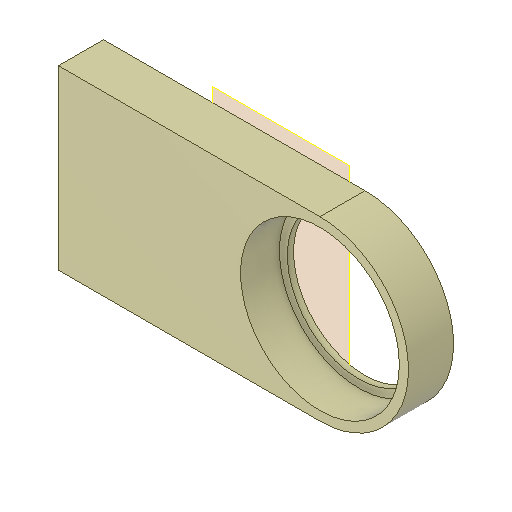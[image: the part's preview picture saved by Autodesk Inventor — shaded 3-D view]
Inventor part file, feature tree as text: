
AUTODESK INVENTOR PART (.ipt)
format: ipt  version: 2022.5 (Build 265521000, 521)  size: 133,632 bytes
history: native  units: mm
features: extrude x2, sketch x2, reference x2, other x2, plane x1, projected_geometry x1
ambient origin geometry x8: Origin, YZ Plane, XZ Plane, XY Plane, X Axis, Y Axis, Z Axis, Center Point
bodies: Solid1 (feature_tree)
feature tree (10):
  plane  "Work Plane1"
  extrude  "Extrusion1"  Depth=25.55mm
  extrude  "Extrusion2"  Depth=1.0mm TaperAngle=0.0deg
  sketch  "Sketch1"  dims[d0=0.75mm d1=25.55mm]
  reference  "Reference1"
  reference  "Reference2"
  sketch  "Sketch2"  dims[d2=23.0mm d3=1.0mm d4=0.0mm d5=25.55mm d6=6.25mm d7=0.0mm]
  projected_geometry  "Projected Loop1"
  other  "Assembly_Axiotech_Eypiece.iam"
  other  "00_Fluegeladapter:1"
